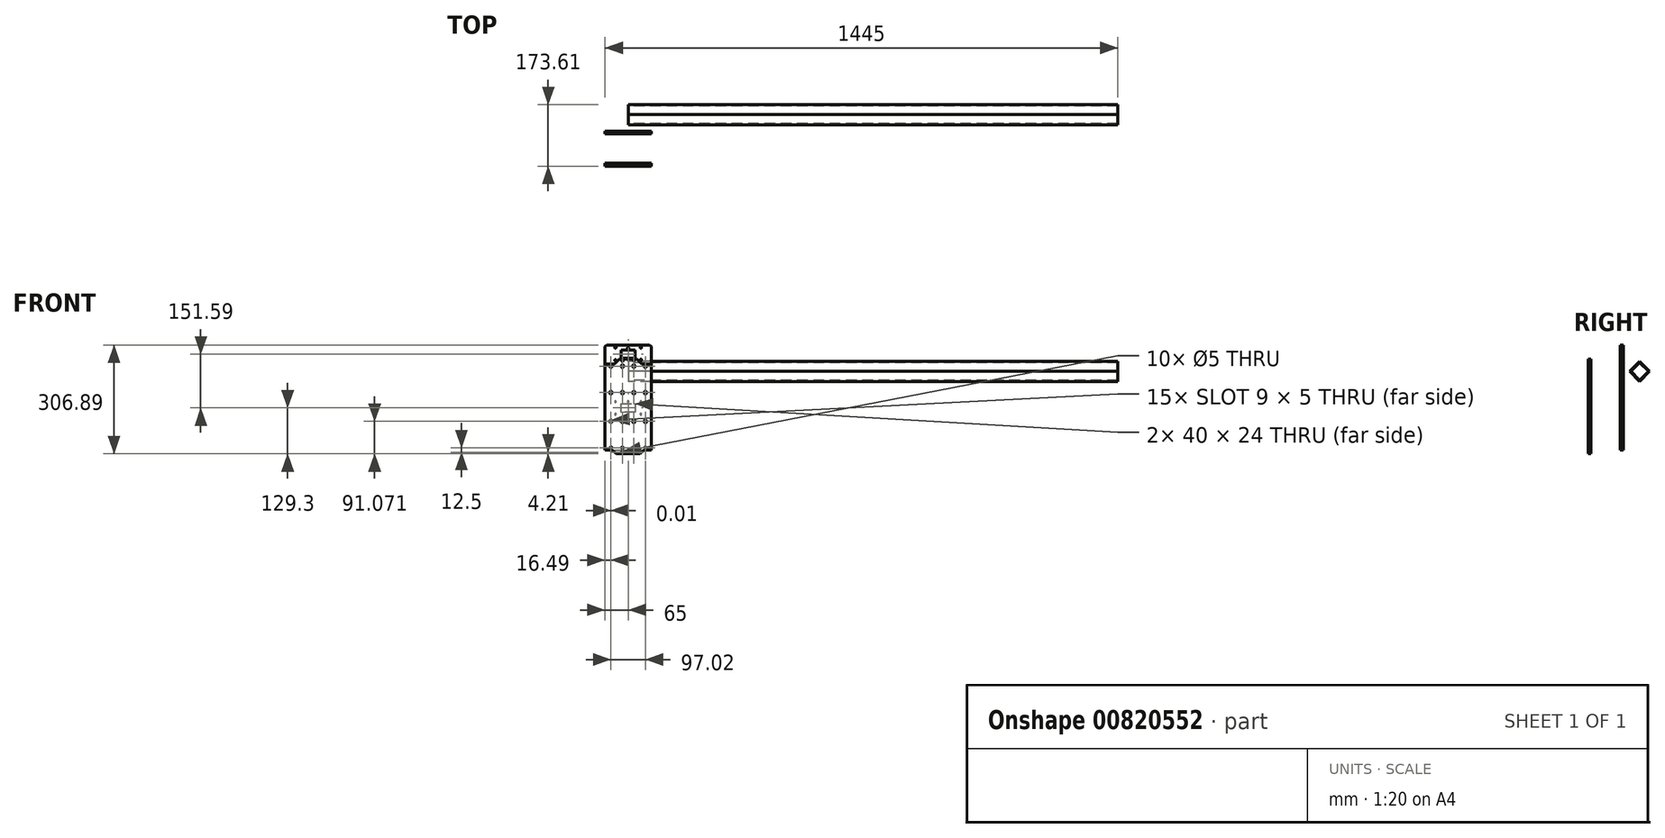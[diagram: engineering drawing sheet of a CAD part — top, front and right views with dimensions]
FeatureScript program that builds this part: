
annotation { "Feature Type Name" : "Feature", "Feature Type Description" : "" }
export const myFeature = defineFeature(function(context is Context, id is Id, definition is map)
    precondition{}
    {
        {
            var Q0;
            Q0=qCreatedBy(makeId("Front.planeOp"),FACE);
            var sketch = newSketch(context, id + "F0", { "sketchPlane" : qUnion([Q0])});
            skLineSegment(sketch, "E0", {"start": v(20, -14.5) * mm, "end": v(-20, -14.5) * mm});
            skLineSegment(sketch, "E1", {"start": v(20, 9.5) * mm, "end": v(20, -14.5) * mm});
            skLineSegment(sketch, "E2", {"start": v(-20, 9.5) * mm, "end": v(20, 9.5) * mm});
            skLineSegment(sketch, "E3", {"start": v(-20, -14.5) * mm, "end": v(-20, 9.5) * mm});
            skLineSegment(sketch, "E4", {"start": v(-51, 50.32) * mm, "end": v(-51, 47.32) * mm});
            skLineSegment(sketch, "E5", {"start": v(-46.01, 47.32) * mm, "end": v(-46.01, 50.32) * mm});
            skLineSegment(sketch, "E6", {"start": v(-18.67, 50.32) * mm, "end": v(-18.67, 47.32) * mm});
            skLineSegment(sketch, "E7", {"start": v(-13.67, 47.32) * mm, "end": v(-13.67, 50.32) * mm});
            skLineSegment(sketch, "E8", {"start": v(13.67, 50.32) * mm, "end": v(13.67, 47.32) * mm});
            skLineSegment(sketch, "E9", {"start": v(18.67, 47.32) * mm, "end": v(18.67, 50.32) * mm});
            skLineSegment(sketch, "E10", {"start": v(46, 50.32) * mm, "end": v(46, 47.32) * mm});
            skLineSegment(sketch, "E11", {"start": v(51, 47.32) * mm, "end": v(51, 50.32) * mm});
            skLineSegment(sketch, "E12", {"start": v(-51, 103.5) * mm, "end": v(-51, 100.5) * mm});
            skLineSegment(sketch, "E13", {"start": v(-46.01, 100.5) * mm, "end": v(-46.01, 103.5) * mm});
            skLineSegment(sketch, "E14", {"start": v(-13.67, 100.5) * mm, "end": v(-13.67, 103.5) * mm});
            skLineSegment(sketch, "E15", {"start": v(-18.67, 103.5) * mm, "end": v(-18.67, 100.5) * mm});
            skLineSegment(sketch, "E16", {"start": v(18.67, 100.5) * mm, "end": v(18.67, 103.5) * mm});
            skLineSegment(sketch, "E17", {"start": v(13.67, 103.5) * mm, "end": v(13.67, 100.5) * mm});
            skLineSegment(sketch, "E18", {"start": v(51, 100.5) * mm, "end": v(51, 103.5) * mm});
            skLineSegment(sketch, "E19", {"start": v(46, 103.5) * mm, "end": v(46, 100.5) * mm});
            skLineSegment(sketch, "E20", {"start": v(-46.01, -55.32) * mm, "end": v(-46.01, -52.32) * mm});
            skLineSegment(sketch, "E21", {"start": v(-51, -52.32) * mm, "end": v(-51, -55.32) * mm});
            skLineSegment(sketch, "E22", {"start": v(-13.67, -55.32) * mm, "end": v(-13.67, -52.32) * mm});
            skLineSegment(sketch, "E23", {"start": v(-18.67, -52.32) * mm, "end": v(-18.67, -55.32) * mm});
            skLineSegment(sketch, "E24", {"start": v(18.67, -55.32) * mm, "end": v(18.67, -52.32) * mm});
            skLineSegment(sketch, "E25", {"start": v(13.67, -52.32) * mm, "end": v(13.67, -55.32) * mm});
            skLineSegment(sketch, "E26", {"start": v(51, -55.32) * mm, "end": v(51, -52.32) * mm});
            skLineSegment(sketch, "E27", {"start": v(46, -52.32) * mm, "end": v(46, -55.32) * mm});
            skLineSegment(sketch, "E28", {"start": v(60, -113.5) * mm, "end": v(65, -108.5) * mm});
            skLineSegment(sketch, "E29", {"start": v(34, -124.5) * mm, "end": v(45, -113.5) * mm});
            skLineSegment(sketch, "E30", {"start": v(34, -124.5) * mm, "end": v(-34, -124.5) * mm});
            skLineSegment(sketch, "E31", {"start": v(-45, -113.5) * mm, "end": v(-34, -124.5) * mm});
            skLineSegment(sketch, "E32", {"start": v(-65, -108.5) * mm, "end": v(-60, -113.5) * mm});
            skLineSegment(sketch, "E33", {"start": v(-60, 110.5) * mm, "end": v(-65, 105.5) * mm});
            skLineSegment(sketch, "E34", {"start": v(-39, 110.5) * mm, "end": v(-60, 110.5) * mm});
            skLineSegment(sketch, "E35", {"start": v(-25, 124.5) * mm, "end": v(-39, 110.5) * mm});
            skLineSegment(sketch, "E36", {"start": v(-25, 124.5) * mm, "end": v(25, 124.5) * mm});
            skLineSegment(sketch, "E37", {"start": v(39, 110.5) * mm, "end": v(25, 124.5) * mm});
            skLineSegment(sketch, "E38", {"start": v(60, 110.5) * mm, "end": v(39, 110.5) * mm});
            skLineSegment(sketch, "E39", {"start": v(65, 105.5) * mm, "end": v(60, 110.5) * mm});
            skLineSegment(sketch, "E40", {"start": v(-65, 105.5) * mm, "end": v(-65, -108.5) * mm});
            skLineSegment(sketch, "E41", {"start": v(65, -108.5) * mm, "end": v(65, 105.5) * mm});
            skLineSegment(sketch, "E42", {"start": v(45, -113.5) * mm, "end": v(60, -113.5) * mm});
            skLineSegment(sketch, "E43", {"start": v(-60, -113.5) * mm, "end": v(-45, -113.5) * mm});
            skCircle(sketch, "E44", {"center": v(-48.5, -107) * mm, "radius": 2.5 * mm});
            skCircle(sketch, "E45", {"center": v(-16.17, -107) * mm, "radius": 2.5 * mm});
            skCircle(sketch, "E46", {"center": v(16.17, -107) * mm, "radius": 2.5 * mm});
            skCircle(sketch, "E47", {"center": v(48.5, -107) * mm, "radius": 2.5 * mm});
            skCircle(sketch, "E48", {"center": v(-36, 15) * mm, "radius": 2.05 * mm});
            skCircle(sketch, "E49", {"center": v(0, 15) * mm, "radius": 2.05 * mm});
            skCircle(sketch, "E50", {"center": v(36, 15) * mm, "radius": 2.05 * mm});
            skCircle(sketch, "E51", {"center": v(36, -20) * mm, "radius": 2.05 * mm});
            skCircle(sketch, "E52", {"center": v(0, -20) * mm, "radius": 2.05 * mm});
            skCircle(sketch, "E53", {"center": v(-36, -20) * mm, "radius": 2.05 * mm});
            skCircle(sketch, "E54", {"center": v(0, 119) * mm, "radius": 2.05 * mm});
            skCircle(sketch, "E55", {"center": v(16.17, -119.5) * mm, "radius": 2.5 * mm});
            skCircle(sketch, "E56", {"center": v(-16.17, -119.5) * mm, "radius": 2.5 * mm});
            skCircle(sketch, "E57", {"center": v(16.17, 119) * mm, "radius": 2.5 * mm});
            skCircle(sketch, "E58", {"center": v(-16.17, 119) * mm, "radius": 2.5 * mm});
            skCircle(sketch, "E59", {"center": v(50, -90) * mm, "radius": 2.25 * mm});
            skCircle(sketch, "E60", {"center": v(50, -65) * mm, "radius": 2.25 * mm});
            skCircle(sketch, "E61", {"center": v(-50, -90) * mm, "radius": 2.25 * mm});
            skCircle(sketch, "E62", {"center": v(-50, -65) * mm, "radius": 2.25 * mm});
            skCircle(sketch, "E63", {"center": v(-50, -40) * mm, "radius": 2.25 * mm});
            skCircle(sketch, "E64", {"center": v(-50, -15) * mm, "radius": 2.25 * mm});
            skCircle(sketch, "E65", {"center": v(50, -40) * mm, "radius": 2.25 * mm});
            skCircle(sketch, "E66", {"center": v(50, -15) * mm, "radius": 2.25 * mm});
            skCircle(sketch, "E67", {"center": v(50, 10) * mm, "radius": 2.25 * mm});
            skCircle(sketch, "E68", {"center": v(-50, 10) * mm, "radius": 2.25 * mm});
            skCircle(sketch, "E69", {"center": v(-50, 35) * mm, "radius": 2.25 * mm});
            skCircle(sketch, "E70", {"center": v(50, 35) * mm, "radius": 2.25 * mm});
            skCircle(sketch, "E71", {"center": v(50, 60) * mm, "radius": 2.25 * mm});
            skCircle(sketch, "E72", {"center": v(-50, 60) * mm, "radius": 2.25 * mm});
            skCircle(sketch, "E73", {"center": v(-50, 85) * mm, "radius": 2.25 * mm});
            skCircle(sketch, "E74", {"center": v(50, 85) * mm, "radius": 2.25 * mm});
            skArc(sketch, "E75", {"start": v(-51, 47.32) * mm, "mid": v(-48.5, 44.82) * mm, "end": v(-46, 47.32) * mm});
            skArc(sketch, "E76", {"start": v(-46, 50.32) * mm, "mid": v(-48.5, 52.82) * mm, "end": v(-51, 50.32) * mm});
            skArc(sketch, "E77", {"start": v(-18.67, 47.32) * mm, "mid": v(-16.17, 44.82) * mm, "end": v(-13.67, 47.32) * mm});
            skArc(sketch, "E78", {"start": v(-13.67, 50.32) * mm, "mid": v(-16.17, 52.82) * mm, "end": v(-18.67, 50.32) * mm});
            skArc(sketch, "E79", {"start": v(13.67, 47.32) * mm, "mid": v(16.17, 44.82) * mm, "end": v(18.67, 47.32) * mm});
            skArc(sketch, "E80", {"start": v(18.67, 50.32) * mm, "mid": v(16.17, 52.82) * mm, "end": v(13.67, 50.32) * mm});
            skArc(sketch, "E81", {"start": v(46, 47.32) * mm, "mid": v(48.5, 44.82) * mm, "end": v(51, 47.32) * mm});
            skArc(sketch, "E82", {"start": v(51, 50.32) * mm, "mid": v(48.5, 52.82) * mm, "end": v(46, 50.32) * mm});
            skArc(sketch, "E83", {"start": v(-51, 100.5) * mm, "mid": v(-48.5, 98) * mm, "end": v(-46, 100.5) * mm});
            skArc(sketch, "E84", {"start": v(-46, 103.5) * mm, "mid": v(-48.5, 106) * mm, "end": v(-51, 103.5) * mm});
            skArc(sketch, "E85", {"start": v(-18.67, 100.5) * mm, "mid": v(-16.17, 98) * mm, "end": v(-13.67, 100.5) * mm});
            skArc(sketch, "E86", {"start": v(-13.67, 103.5) * mm, "mid": v(-16.17, 106) * mm, "end": v(-18.67, 103.5) * mm});
            skArc(sketch, "E87", {"start": v(13.67, 100.5) * mm, "mid": v(16.17, 98) * mm, "end": v(18.67, 100.5) * mm});
            skArc(sketch, "E88", {"start": v(18.67, 103.5) * mm, "mid": v(16.17, 106) * mm, "end": v(13.67, 103.5) * mm});
            skArc(sketch, "E89", {"start": v(46, 100.5) * mm, "mid": v(48.5, 98) * mm, "end": v(51, 100.5) * mm});
            skArc(sketch, "E90", {"start": v(51, 103.5) * mm, "mid": v(48.5, 106) * mm, "end": v(46, 103.5) * mm});
            skArc(sketch, "E91", {"start": v(-51, -55.32) * mm, "mid": v(-48.5, -57.82) * mm, "end": v(-46, -55.32) * mm});
            skArc(sketch, "E92", {"start": v(-46, -52.32) * mm, "mid": v(-48.5, -49.82) * mm, "end": v(-51, -52.32) * mm});
            skArc(sketch, "E93", {"start": v(-18.67, -55.32) * mm, "mid": v(-16.17, -57.82) * mm, "end": v(-13.67, -55.32) * mm});
            skArc(sketch, "E94", {"start": v(-13.67, -52.32) * mm, "mid": v(-16.17, -49.82) * mm, "end": v(-18.67, -52.32) * mm});
            skArc(sketch, "E95", {"start": v(13.67, -55.32) * mm, "mid": v(16.17, -57.82) * mm, "end": v(18.67, -55.32) * mm});
            skArc(sketch, "E96", {"start": v(18.67, -52.32) * mm, "mid": v(16.17, -49.82) * mm, "end": v(13.67, -52.32) * mm});
            skArc(sketch, "E97", {"start": v(46, -55.32) * mm, "mid": v(48.5, -57.82) * mm, "end": v(51, -55.32) * mm});
            skArc(sketch, "E98", {"start": v(51, -52.32) * mm, "mid": v(48.5, -49.82) * mm, "end": v(46, -52.32) * mm});
            skSolve(sketch);
        }
        {
            var Q0;
            Q0=qCreatedBy(makeId("Right.planeOp"),FACE);
            var sketch = newSketch(context, id + "F1", { "sketchPlane" : qUnion([Q0])});
            skLineSegment(sketch, "E99.bottom", {"start": v(137.33, 128.79) * mm, "end": v(109.04, 100.5) * mm});
            skLineSegment(sketch, "E99.top", {"start": v(165.61, 100.5) * mm, "end": v(137.33, 72.22) * mm});
            skLineSegment(sketch, "E99.left", {"start": v(137.33, 128.79) * mm, "end": v(165.61, 100.5) * mm});
            skLineSegment(sketch, "E99.right", {"start": v(109.04, 100.5) * mm, "end": v(137.33, 72.22) * mm});
            skSolve(sketch);
        }
        {
            var Q0;
            Q0=qSketchRegion(id+"F1",true);
            extrude(context, id + "F2", {"entities" : qUnion([Q0]), "depth" : 1380 * mm, "offsetDistance" : 25 * mm});
        }
        {
            var Q0;
            Q0=makeQuery(id+"F2.opExtrude","CAP_FACE",FACE,{"disambiguationData":[OSD([sQuery(id+"F1.wireOp",EDGE,"E99.bottom"),sQuery(id+"F1.wireOp",EDGE,"E99.top"),sQuery(id+"F1.wireOp",EDGE,"E99.left"),sQuery(id+"F1.wireOp",EDGE,"E99.right")])],"isStart":true});
            var Q1;
            Q1=makeQuery(id+"F2.opExtrude","CAP_FACE",FACE,{"disambiguationData":[OSD([sQuery(id+"F1.wireOp",EDGE,"E99.bottom"),sQuery(id+"F1.wireOp",EDGE,"E99.top"),sQuery(id+"F1.wireOp",EDGE,"E99.left"),sQuery(id+"F1.wireOp",EDGE,"E99.right")])],"isStart":false});
            shell(context, id + "F3", {"entities" : qUnion([Q0, Q1]), "thickness" : 2.5 * mm});
        }
        {
            var Q0;
            Q0=qCreatedBy(makeId("Front.planeOp"),FACE);
            var sketch = newSketch(context, id + "F4", { "sketchPlane" : qUnion([Q0])});
            skLineSegment(sketch, "E100.bottom", {"start": v(65, 121.7) * mm, "end": v(-65, 121.7) * mm});
            skLineSegment(sketch, "E100.left", {"start": v(65, 121.7) * mm, "end": v(65, -121.7) * mm});
            skLineSegment(sketch, "E100.right", {"start": v(-65, 121.7) * mm, "end": v(-65, -121.7) * mm});
            skCircle(sketch, "E101", {"center": v(-48.5, -115.1) * mm, "radius": 2.5 * mm});
            skCircle(sketch, "E102", {"center": v(-16.18, -115.1) * mm, "radius": 2.5 * mm});
            skCircle(sketch, "E103", {"center": v(16.18, -115.1) * mm, "radius": 2.5 * mm});
            skCircle(sketch, "E104", {"center": v(48.5, -115.1) * mm, "radius": 2.5 * mm});
            skLineSegment(sketch, "E105", {"start": v(-48.5, -42.51) * mm, "end": v(-48.5, -38.51) * mm});
            skLineSegment(sketch, "E106", {"start": v(-16.18, -42.51) * mm, "end": v(-16.18, -38.51) * mm});
            skLineSegment(sketch, "E107", {"start": v(16.18, -42.51) * mm, "end": v(16.18, -38.51) * mm});
            skLineSegment(sketch, "E108", {"start": v(48.5, -42.51) * mm, "end": v(48.5, -38.51) * mm});
            skLineSegment(sketch, "E109.MirrorCS", {"start": v(16.18, 42.51) * mm, "end": v(16.18, 38.51) * mm});
            skLineSegment(sketch, "E110.MirrorCS", {"start": v(48.5, 42.51) * mm, "end": v(48.5, 38.51) * mm});
            skLineSegment(sketch, "E111.MirrorCS", {"start": v(-16.18, 42.51) * mm, "end": v(-16.18, 38.51) * mm});
            skLineSegment(sketch, "E112.MirrorCS", {"start": v(-48.5, 42.51) * mm, "end": v(-48.5, 38.51) * mm});
            skLineSegment(sketch, "E113", {"start": v(-48.5, 117.1) * mm, "end": v(-48.5, 113.1) * mm});
            skLineSegment(sketch, "E114", {"start": v(-16.18, 117.1) * mm, "end": v(-16.18, 113.1) * mm});
            skLineSegment(sketch, "E115", {"start": v(16.18, 117.1) * mm, "end": v(16.18, 113.1) * mm});
            skLineSegment(sketch, "E116", {"start": v(48.5, 117.1) * mm, "end": v(48.5, 113.1) * mm});
            skArc(sketch, "E117.0.startCap", {"start": v(-51, 117.1) * mm, "mid": v(-48.5, 119.6) * mm, "end": v(-46, 117.1) * mm});
            skArc(sketch, "E117.0.endCap", {"start": v(-46, 113.1) * mm, "mid": v(-48.5, 110.6) * mm, "end": v(-51, 113.1) * mm});
            skLineSegment(sketch, "E117.0.left", {"start": v(-46, 117.1) * mm, "end": v(-46, 113.1) * mm});
            skLineSegment(sketch, "E117.0.right", {"start": v(-51, 117.1) * mm, "end": v(-51, 113.1) * mm});
            skArc(sketch, "E117.1.startCap", {"start": v(-18.68, 117.1) * mm, "mid": v(-16.18, 119.6) * mm, "end": v(-13.68, 117.1) * mm});
            skArc(sketch, "E117.1.endCap", {"start": v(-13.68, 113.1) * mm, "mid": v(-16.18, 110.6) * mm, "end": v(-18.68, 113.1) * mm});
            skLineSegment(sketch, "E117.1.left", {"start": v(-13.68, 117.1) * mm, "end": v(-13.68, 113.1) * mm});
            skLineSegment(sketch, "E117.1.right", {"start": v(-18.68, 117.1) * mm, "end": v(-18.68, 113.1) * mm});
            skArc(sketch, "E117.2.startCap", {"start": v(13.68, 117.1) * mm, "mid": v(16.18, 119.6) * mm, "end": v(18.68, 117.1) * mm});
            skArc(sketch, "E117.2.endCap", {"start": v(18.68, 113.1) * mm, "mid": v(16.18, 110.6) * mm, "end": v(13.68, 113.1) * mm});
            skLineSegment(sketch, "E117.2.left", {"start": v(18.68, 117.1) * mm, "end": v(18.68, 113.1) * mm});
            skLineSegment(sketch, "E117.2.right", {"start": v(13.68, 117.1) * mm, "end": v(13.68, 113.1) * mm});
            skArc(sketch, "E117.3.startCap", {"start": v(46, 117.1) * mm, "mid": v(48.5, 119.6) * mm, "end": v(51, 117.1) * mm});
            skArc(sketch, "E117.3.endCap", {"start": v(51, 113.1) * mm, "mid": v(48.5, 110.6) * mm, "end": v(46, 113.1) * mm});
            skLineSegment(sketch, "E117.3.left", {"start": v(51, 117.1) * mm, "end": v(51, 113.1) * mm});
            skLineSegment(sketch, "E117.3.right", {"start": v(46, 117.1) * mm, "end": v(46, 113.1) * mm});
            skArc(sketch, "E117.4.startCap", {"start": v(-51, 42.51) * mm, "mid": v(-48.5, 45.01) * mm, "end": v(-46, 42.51) * mm});
            skArc(sketch, "E117.4.endCap", {"start": v(-46, 38.51) * mm, "mid": v(-48.5, 36.01) * mm, "end": v(-51, 38.51) * mm});
            skLineSegment(sketch, "E117.4.left", {"start": v(-46, 42.51) * mm, "end": v(-46, 38.51) * mm});
            skLineSegment(sketch, "E117.4.right", {"start": v(-51, 42.51) * mm, "end": v(-51, 38.51) * mm});
            skArc(sketch, "E117.5.startCap", {"start": v(-18.68, 42.51) * mm, "mid": v(-16.18, 45.01) * mm, "end": v(-13.68, 42.51) * mm});
            skArc(sketch, "E117.5.endCap", {"start": v(-13.68, 38.51) * mm, "mid": v(-16.18, 36.01) * mm, "end": v(-18.68, 38.51) * mm});
            skLineSegment(sketch, "E117.5.left", {"start": v(-13.68, 42.51) * mm, "end": v(-13.68, 38.51) * mm});
            skLineSegment(sketch, "E117.5.right", {"start": v(-18.68, 42.51) * mm, "end": v(-18.68, 38.51) * mm});
            skArc(sketch, "E117.6.startCap", {"start": v(13.68, 42.51) * mm, "mid": v(16.18, 45.01) * mm, "end": v(18.68, 42.51) * mm});
            skArc(sketch, "E117.6.endCap", {"start": v(18.68, 38.51) * mm, "mid": v(16.18, 36.01) * mm, "end": v(13.68, 38.51) * mm});
            skLineSegment(sketch, "E117.6.left", {"start": v(18.68, 42.51) * mm, "end": v(18.68, 38.51) * mm});
            skLineSegment(sketch, "E117.6.right", {"start": v(13.68, 42.51) * mm, "end": v(13.68, 38.51) * mm});
            skArc(sketch, "E117.7.startCap", {"start": v(46, 42.51) * mm, "mid": v(48.5, 45.01) * mm, "end": v(51, 42.51) * mm});
            skArc(sketch, "E117.7.endCap", {"start": v(51, 38.51) * mm, "mid": v(48.5, 36.01) * mm, "end": v(46, 38.51) * mm});
            skLineSegment(sketch, "E117.7.left", {"start": v(51, 42.51) * mm, "end": v(51, 38.51) * mm});
            skLineSegment(sketch, "E117.7.right", {"start": v(46, 42.51) * mm, "end": v(46, 38.51) * mm});
            skArc(sketch, "E117.8.startCap", {"start": v(51, -42.51) * mm, "mid": v(48.5, -45.01) * mm, "end": v(46, -42.51) * mm});
            skArc(sketch, "E117.8.endCap", {"start": v(46, -38.51) * mm, "mid": v(48.5, -36.01) * mm, "end": v(51, -38.51) * mm});
            skLineSegment(sketch, "E117.8.left", {"start": v(46, -42.51) * mm, "end": v(46, -38.51) * mm});
            skLineSegment(sketch, "E117.8.right", {"start": v(51, -42.51) * mm, "end": v(51, -38.51) * mm});
            skArc(sketch, "E117.9.startCap", {"start": v(18.68, -42.51) * mm, "mid": v(16.18, -45.01) * mm, "end": v(13.68, -42.51) * mm});
            skArc(sketch, "E117.9.endCap", {"start": v(13.68, -38.51) * mm, "mid": v(16.18, -36.01) * mm, "end": v(18.68, -38.51) * mm});
            skLineSegment(sketch, "E117.9.left", {"start": v(13.68, -42.51) * mm, "end": v(13.68, -38.51) * mm});
            skLineSegment(sketch, "E117.9.right", {"start": v(18.68, -42.51) * mm, "end": v(18.68, -38.51) * mm});
            skArc(sketch, "E117.10.startCap", {"start": v(-13.68, -42.51) * mm, "mid": v(-16.18, -45.01) * mm, "end": v(-18.68, -42.51) * mm});
            skArc(sketch, "E117.10.endCap", {"start": v(-18.68, -38.51) * mm, "mid": v(-16.18, -36.01) * mm, "end": v(-13.68, -38.51) * mm});
            skLineSegment(sketch, "E117.10.left", {"start": v(-18.68, -42.51) * mm, "end": v(-18.68, -38.51) * mm});
            skLineSegment(sketch, "E117.10.right", {"start": v(-13.68, -42.51) * mm, "end": v(-13.68, -38.51) * mm});
            skArc(sketch, "E117.11.startCap", {"start": v(-46, -42.51) * mm, "mid": v(-48.5, -45.01) * mm, "end": v(-51, -42.51) * mm});
            skArc(sketch, "E117.11.endCap", {"start": v(-51, -38.51) * mm, "mid": v(-48.5, -36.01) * mm, "end": v(-46, -38.51) * mm});
            skLineSegment(sketch, "E117.11.left", {"start": v(-51, -42.51) * mm, "end": v(-51, -38.51) * mm});
            skLineSegment(sketch, "E117.11.right", {"start": v(-46, -42.51) * mm, "end": v(-46, -38.51) * mm});
            skLineSegment(sketch, "E118", {"start": v(-39, 121.7) * mm, "end": v(-25, 135.7) * mm});
            skLineSegment(sketch, "E119", {"start": v(-25, 135.7) * mm, "end": v(25, 135.7) * mm});
            skLineSegment(sketch, "E120", {"start": v(25, 135.7) * mm, "end": v(39, 121.7) * mm});
            skLineSegment(sketch, "E121", {"start": v(39, 121.7) * mm, "end": v(39, 103.73) * mm, "construction": true});
            skLineSegment(sketch, "E122", {"start": v(25, 135.7) * mm, "end": v(25, 118.95) * mm, "construction": true});
            skLineSegment(sketch, "E123", {"start": v(-25, 135.7) * mm, "end": v(-25, 118.52) * mm, "construction": true});
            skLineSegment(sketch, "E124", {"start": v(-39, 121.7) * mm, "end": v(-39, 105.53) * mm, "construction": true});
            skLineSegment(sketch, "E125", {"start": v(-45, -121.7) * mm, "end": v(-45, -110.8) * mm, "construction": true});
            skLineSegment(sketch, "E126", {"start": v(-34, -131.8) * mm, "end": v(-34, -118.6) * mm, "construction": true});
            skLineSegment(sketch, "E127", {"start": v(34, -131.8) * mm, "end": v(34, -118.8) * mm, "construction": true});
            skLineSegment(sketch, "E128", {"start": v(45, -121.7) * mm, "end": v(45, -111) * mm, "construction": true});
            skCircle(sketch, "E129", {"center": v(-16.18, -127.6) * mm, "radius": 2.5 * mm});
            skCircle(sketch, "E130", {"center": v(16.18, -127.6) * mm, "radius": 2.5 * mm});
            skLineSegment(sketch, "E131", {"start": v(-65, -121.7) * mm, "end": v(-45, -121.7) * mm});
            skLineSegment(sketch, "E132", {"start": v(-34, -131.8) * mm, "end": v(-45, -121.7) * mm});
            skLineSegment(sketch, "E133", {"start": v(-34, -131.8) * mm, "end": v(34, -131.8) * mm});
            skLineSegment(sketch, "E134", {"start": v(34, -131.8) * mm, "end": v(45, -121.7) * mm});
            skLineSegment(sketch, "E135", {"start": v(45, -121.7) * mm, "end": v(65, -121.7) * mm});
            skCircle(sketch, "E136", {"center": v(-16.18, 130.74) * mm, "radius": 2.57 * mm});
            skCircle(sketch, "E137", {"center": v(16.18, 132.1) * mm, "radius": 2.49 * mm});
            skSolve(sketch);
        }
        {
            var Q0;
            Q0=makeQuery(id+"F4.imprint","IMPRINT",FACE,{"disambiguationData":[TD([[makeQuery(id+"F4.imprint","IMPRINT",EDGE,{"derivedFrom":sQuery(id+"F4.wireOp",EDGE,"E100.bottom")}),1.0]])]});
            var Q1;
            {var subQ0=sQuery(id+"F4.wireOp",EDGE,"E118");Q1=makeQuery(id+"F4.imprint","IMPRINT",FACE,{"disambiguationData":[TD([[makeQuery(id+"F4.imprint","IMPRINT",EDGE,{"derivedFrom":subQ0}),-1.0]])]});}
            var Q2;
            {var subQ0=sQuery(id+"F4.wireOp",EDGE,"JYC6ol7t-ZKkB-sm1I-73n9-ntt4Y6ct0uzj");Q2=makeQuery(id+"F4.imprint","IMPRINT",FACE,{"disambiguationData":[TD([[makeQuery(id+"F4.imprint","IMPRINT",EDGE,{"derivedFrom":subQ0}),1.0]])]});}
            extrude(context, id + "F5", {"entities" : qUnion([Q0, Q1, Q2]), "depth" : 8 * mm, "offsetDistance" : 25 * mm});
        }
        {
            var Q0;
            Q0=qCreatedBy(makeId("Front.planeOp"),FACE);
            cPlane(context, id + "F6", {"entities" : qUnion([Q0]), "cplaneType" : CPlaneType.OFFSET, "offset" : 83 * mm, "oppositeDirection" : true, "width" : 150 * mm, "height" : 150 * mm});
        }
        {
            var Q0;
            Q0=qCreatedBy(id+"F6.planeOp",FACE);
            var sketch = newSketch(context, id + "F7", { "sketchPlane" : qUnion([Q0])});
            skLineSegment(sketch, "E138", {"start": v(-60, 175.1) * mm, "end": v(-65, 170.1) * mm});
            skLineSegment(sketch, "E139", {"start": v(60, 175.1) * mm, "end": v(-60, 175.1) * mm});
            skLineSegment(sketch, "E140", {"start": v(65, 170.1) * mm, "end": v(60, 175.1) * mm});
            skLineSegment(sketch, "E141", {"start": v(60, -121.7) * mm, "end": v(65, -116.7) * mm});
            skLineSegment(sketch, "E142", {"start": v(-65, -116.7) * mm, "end": v(-60, -121.7) * mm});
            skLineSegment(sketch, "E143", {"start": v(20, -14.5) * mm, "end": v(-20, -14.5) * mm});
            skLineSegment(sketch, "E144", {"start": v(20, 9.5) * mm, "end": v(20, -14.5) * mm});
            skLineSegment(sketch, "E145", {"start": v(-20, 9.5) * mm, "end": v(20, 9.5) * mm});
            skLineSegment(sketch, "E146", {"start": v(-20, -14.5) * mm, "end": v(-20, 9.5) * mm});
            skLineSegment(sketch, "E147", {"start": v(-51, 42.51) * mm, "end": v(-51, 38.51) * mm});
            skLineSegment(sketch, "E148", {"start": v(-46, 38.51) * mm, "end": v(-46, 42.51) * mm});
            skLineSegment(sketch, "E149", {"start": v(-18.67, 42.51) * mm, "end": v(-18.67, 38.51) * mm});
            skLineSegment(sketch, "E150", {"start": v(-13.67, 38.51) * mm, "end": v(-13.67, 42.51) * mm});
            skLineSegment(sketch, "E151", {"start": v(13.67, 42.51) * mm, "end": v(13.67, 38.51) * mm});
            skLineSegment(sketch, "E152", {"start": v(18.67, 38.51) * mm, "end": v(18.67, 42.51) * mm});
            skLineSegment(sketch, "E153", {"start": v(46, 42.51) * mm, "end": v(46, 38.51) * mm});
            skLineSegment(sketch, "E154", {"start": v(51, 38.51) * mm, "end": v(51, 42.51) * mm});
            skLineSegment(sketch, "E155", {"start": v(-51, 117.1) * mm, "end": v(-51, 113.09) * mm});
            skLineSegment(sketch, "E156", {"start": v(-46, 113.09) * mm, "end": v(-46, 117.1) * mm});
            skLineSegment(sketch, "E157", {"start": v(-13.67, 113.09) * mm, "end": v(-13.67, 117.1) * mm});
            skLineSegment(sketch, "E158", {"start": v(-18.67, 117.1) * mm, "end": v(-18.67, 113.09) * mm});
            skLineSegment(sketch, "E159", {"start": v(18.67, 113.09) * mm, "end": v(18.67, 117.1) * mm});
            skLineSegment(sketch, "E160", {"start": v(13.67, 117.1) * mm, "end": v(13.67, 113.09) * mm});
            skLineSegment(sketch, "E161", {"start": v(51, 113.09) * mm, "end": v(51, 117.1) * mm});
            skLineSegment(sketch, "E162", {"start": v(46, 117.1) * mm, "end": v(46, 113.1) * mm});
            skLineSegment(sketch, "E163", {"start": v(-46, -42.73) * mm, "end": v(-46, -38.73) * mm});
            skLineSegment(sketch, "E164", {"start": v(-51, -38.73) * mm, "end": v(-51, -42.73) * mm});
            skLineSegment(sketch, "E165", {"start": v(-13.67, -42.73) * mm, "end": v(-13.67, -38.73) * mm});
            skLineSegment(sketch, "E166", {"start": v(-18.67, -38.73) * mm, "end": v(-18.67, -42.73) * mm});
            skLineSegment(sketch, "E167", {"start": v(18.67, -42.73) * mm, "end": v(18.67, -38.73) * mm});
            skLineSegment(sketch, "E168", {"start": v(13.67, -38.73) * mm, "end": v(13.67, -42.73) * mm});
            skLineSegment(sketch, "E169", {"start": v(51, -42.73) * mm, "end": v(51, -38.73) * mm});
            skLineSegment(sketch, "E170", {"start": v(46, -38.73) * mm, "end": v(46, -42.73) * mm});
            skLineSegment(sketch, "E171", {"start": v(20, 161.1) * mm, "end": v(-20, 161.1) * mm});
            skLineSegment(sketch, "E172", {"start": v(-20, 161.1) * mm, "end": v(-20, 137.1) * mm});
            skLineSegment(sketch, "E173", {"start": v(-20, 137.1) * mm, "end": v(20, 137.1) * mm});
            skLineSegment(sketch, "E174", {"start": v(20, 137.1) * mm, "end": v(20, 161.09) * mm});
            skLineSegment(sketch, "E175", {"start": v(-65, 170.1) * mm, "end": v(-65, -116.7) * mm});
            skLineSegment(sketch, "E176", {"start": v(65, -116.7) * mm, "end": v(65, 170.09) * mm});
            skLineSegment(sketch, "E177", {"start": v(-60, -121.7) * mm, "end": v(60, -121.7) * mm});
            skCircle(sketch, "E178", {"center": v(-48.5, -115.2) * mm, "radius": 2.5 * mm});
            skCircle(sketch, "E179", {"center": v(-16.17, -115.2) * mm, "radius": 2.5 * mm});
            skCircle(sketch, "E180", {"center": v(16.17, -115.2) * mm, "radius": 2.5 * mm});
            skCircle(sketch, "E181", {"center": v(48.5, -115.2) * mm, "radius": 2.5 * mm});
            skCircle(sketch, "E182", {"center": v(-36, 15) * mm, "radius": 2.05 * mm});
            skCircle(sketch, "E183", {"center": v(0, 15) * mm, "radius": 2.05 * mm});
            skCircle(sketch, "E184", {"center": v(36, 15) * mm, "radius": 2.05 * mm});
            skCircle(sketch, "E185", {"center": v(36, -20) * mm, "radius": 2.05 * mm});
            skCircle(sketch, "E186", {"center": v(0, -20) * mm, "radius": 2.05 * mm});
            skCircle(sketch, "E187", {"center": v(-36, -20) * mm, "radius": 2.05 * mm});
            skCircle(sketch, "E188", {"center": v(-36, 167.6) * mm, "radius": 2.05 * mm});
            skCircle(sketch, "E189", {"center": v(0, 166.6) * mm, "radius": 2.05 * mm});
            skCircle(sketch, "E190", {"center": v(36, 167.6) * mm, "radius": 2.05 * mm});
            skCircle(sketch, "E191", {"center": v(36, 132.6) * mm, "radius": 2.05 * mm});
            skCircle(sketch, "E192", {"center": v(0, 131.59) * mm, "radius": 2.05 * mm});
            skCircle(sketch, "E193", {"center": v(-36, 131.59) * mm, "radius": 2.05 * mm});
            skArc(sketch, "E194", {"start": v(-51, 38.51) * mm, "mid": v(-48.5, 36.01) * mm, "end": v(-46, 38.51) * mm});
            skArc(sketch, "E195", {"start": v(-45.97, 42.51) * mm, "mid": v(-48.47, 45.01) * mm, "end": v(-50.97, 42.51) * mm});
            skArc(sketch, "E196", {"start": v(-18.67, 38.51) * mm, "mid": v(-16.17, 36.01) * mm, "end": v(-13.67, 38.51) * mm});
            skArc(sketch, "E197", {"start": v(-13.64, 42.51) * mm, "mid": v(-16.14, 45.01) * mm, "end": v(-18.64, 42.51) * mm});
            skArc(sketch, "E198", {"start": v(13.67, 38.51) * mm, "mid": v(16.17, 36.01) * mm, "end": v(18.67, 38.51) * mm});
            skArc(sketch, "E199", {"start": v(18.7, 42.51) * mm, "mid": v(16.2, 45.01) * mm, "end": v(13.7, 42.51) * mm});
            skArc(sketch, "E200", {"start": v(46.01, 38.51) * mm, "mid": v(48.51, 36.01) * mm, "end": v(51, 38.51) * mm});
            skArc(sketch, "E201", {"start": v(51.05, 42.51) * mm, "mid": v(48.55, 45.01) * mm, "end": v(46.05, 42.51) * mm});
            skArc(sketch, "E202", {"start": v(-51, 113.1) * mm, "mid": v(-48.5, 110.6) * mm, "end": v(-46, 113.1) * mm});
            skArc(sketch, "E203", {"start": v(-46, 117.1) * mm, "mid": v(-48.5, 119.6) * mm, "end": v(-51, 117.1) * mm});
            skArc(sketch, "E204", {"start": v(-18.67, 113.1) * mm, "mid": v(-16.17, 110.6) * mm, "end": v(-13.67, 113.1) * mm});
            skArc(sketch, "E205", {"start": v(-13.67, 117.1) * mm, "mid": v(-16.17, 119.6) * mm, "end": v(-18.67, 117.1) * mm});
            skArc(sketch, "E206", {"start": v(13.68, 113.1) * mm, "mid": v(16.18, 110.6) * mm, "end": v(18.68, 113.1) * mm});
            skArc(sketch, "E207", {"start": v(18.65, 117.1) * mm, "mid": v(16.15, 119.6) * mm, "end": v(13.65, 117.1) * mm});
            skArc(sketch, "E208", {"start": v(46, 113.1) * mm, "mid": v(48.5, 110.6) * mm, "end": v(51, 113.1) * mm});
            skArc(sketch, "E209", {"start": v(51, 117.1) * mm, "mid": v(48.5, 119.6) * mm, "end": v(46, 117.1) * mm});
            skArc(sketch, "E210", {"start": v(-51, -42.73) * mm, "mid": v(-48.5, -45.23) * mm, "end": v(-46, -42.73) * mm});
            skArc(sketch, "E211", {"start": v(-46.02, -38.73) * mm, "mid": v(-48.52, -36.23) * mm, "end": v(-51.02, -38.73) * mm});
            skArc(sketch, "E212", {"start": v(-18.67, -42.73) * mm, "mid": v(-16.17, -45.23) * mm, "end": v(-13.67, -42.73) * mm});
            skArc(sketch, "E213", {"start": v(-13.68, -38.73) * mm, "mid": v(-16.18, -36.23) * mm, "end": v(-18.68, -38.73) * mm});
            skArc(sketch, "E214", {"start": v(13.67, -42.73) * mm, "mid": v(16.17, -45.23) * mm, "end": v(18.67, -42.73) * mm});
            skArc(sketch, "E215", {"start": v(18.65, -38.73) * mm, "mid": v(16.15, -36.23) * mm, "end": v(13.65, -38.73) * mm});
            skArc(sketch, "E216", {"start": v(45.97, -42.73) * mm, "mid": v(48.47, -45.23) * mm, "end": v(50.97, -42.73) * mm});
            skArc(sketch, "E217", {"start": v(51, -38.73) * mm, "mid": v(48.5, -36.23) * mm, "end": v(46, -38.73) * mm});
            skLineSegment(sketch, "E218.bottom", {"start": v(46, 117.1) * mm, "end": v(51, 117.1) * mm});
            skLineSegment(sketch, "E218.top", {"start": v(46, 113.1) * mm, "end": v(51, 113.1) * mm});
            skLineSegment(sketch, "E218.right", {"start": v(51, 117.1) * mm, "end": v(51, 113.1) * mm});
            skLineSegment(sketch, "E219.bottom", {"start": v(13.67, 117.1) * mm, "end": v(18.68, 117.1) * mm});
            skLineSegment(sketch, "E219.top", {"start": v(13.67, 113.1) * mm, "end": v(18.68, 113.1) * mm});
            skLineSegment(sketch, "E219.left", {"start": v(13.67, 117.1) * mm, "end": v(13.67, 113.1) * mm});
            skLineSegment(sketch, "E219.right", {"start": v(18.68, 117.1) * mm, "end": v(18.68, 113.1) * mm});
            skLineSegment(sketch, "E220.bottom", {"start": v(-18.67, 117.1) * mm, "end": v(-13.67, 117.1) * mm});
            skLineSegment(sketch, "E220.top", {"start": v(-18.67, 113.1) * mm, "end": v(-13.67, 113.1) * mm});
            skLineSegment(sketch, "E220.left", {"start": v(-18.67, 117.1) * mm, "end": v(-18.67, 113.1) * mm});
            skLineSegment(sketch, "E220.right", {"start": v(-13.67, 117.1) * mm, "end": v(-13.67, 113.1) * mm});
            skLineSegment(sketch, "E221.bottom", {"start": v(-51, 117.1) * mm, "end": v(-46, 117.1) * mm});
            skLineSegment(sketch, "E221.top", {"start": v(-51, 113.1) * mm, "end": v(-46, 113.1) * mm});
            skLineSegment(sketch, "E221.left", {"start": v(-51, 117.1) * mm, "end": v(-51, 113.1) * mm});
            skLineSegment(sketch, "E221.right", {"start": v(-46, 117.1) * mm, "end": v(-46, 113.1) * mm});
            skCircle(sketch, "E222", {"center": v(-48.5, 117.1) * mm, "radius": 2.5 * mm});
            skCircle(sketch, "E223", {"center": v(-48.5, 113.1) * mm, "radius": 2.5 * mm});
            skCircle(sketch, "E224", {"center": v(-16.17, 117.1) * mm, "radius": 2.5 * mm});
            skCircle(sketch, "E225", {"center": v(-16.17, 113.1) * mm, "radius": 2.5 * mm});
            skCircle(sketch, "E226", {"center": v(16.15, 117.1) * mm, "radius": 2.5 * mm});
            skCircle(sketch, "E227", {"center": v(16.18, 113.1) * mm, "radius": 2.5 * mm});
            skCircle(sketch, "E228", {"center": v(48.5, 117.1) * mm, "radius": 2.5 * mm});
            skCircle(sketch, "E229", {"center": v(48.5, 113.1) * mm, "radius": 2.5 * mm});
            skLineSegment(sketch, "E230.bottom", {"start": v(-50.97, 42.51) * mm, "end": v(-46, 42.51) * mm});
            skLineSegment(sketch, "E230.top", {"start": v(-50.97, 38.51) * mm, "end": v(-46, 38.51) * mm});
            skLineSegment(sketch, "E230.left", {"start": v(-50.97, 42.51) * mm, "end": v(-50.97, 38.51) * mm});
            skLineSegment(sketch, "E230.right", {"start": v(-46, 42.51) * mm, "end": v(-46, 38.51) * mm});
            skLineSegment(sketch, "E231.bottom", {"start": v(-18.64, 42.51) * mm, "end": v(-13.67, 42.51) * mm});
            skLineSegment(sketch, "E231.top", {"start": v(-18.64, 38.51) * mm, "end": v(-13.67, 38.51) * mm});
            skLineSegment(sketch, "E231.left", {"start": v(-18.64, 42.51) * mm, "end": v(-18.64, 38.51) * mm});
            skLineSegment(sketch, "E231.right", {"start": v(-13.67, 42.51) * mm, "end": v(-13.67, 38.51) * mm});
            skLineSegment(sketch, "E232.bottom", {"start": v(13.7, 42.51) * mm, "end": v(18.67, 42.51) * mm});
            skLineSegment(sketch, "E232.top", {"start": v(13.7, 38.51) * mm, "end": v(18.67, 38.51) * mm});
            skLineSegment(sketch, "E232.left", {"start": v(13.7, 42.51) * mm, "end": v(13.7, 38.51) * mm});
            skLineSegment(sketch, "E232.right", {"start": v(18.67, 42.51) * mm, "end": v(18.67, 38.51) * mm});
            skLineSegment(sketch, "E233.bottom", {"start": v(46.05, 42.51) * mm, "end": v(51, 42.51) * mm});
            skLineSegment(sketch, "E233.top", {"start": v(46.05, 38.51) * mm, "end": v(51, 38.51) * mm});
            skLineSegment(sketch, "E233.left", {"start": v(46.05, 42.51) * mm, "end": v(46.05, 38.51) * mm});
            skLineSegment(sketch, "E233.right", {"start": v(51, 42.51) * mm, "end": v(51, 38.51) * mm});
            skCircle(sketch, "E234", {"center": v(-48.47, 42.51) * mm, "radius": 2.5 * mm});
            skCircle(sketch, "E235", {"center": v(-48.5, 38.51) * mm, "radius": 2.5 * mm});
            skCircle(sketch, "E236", {"center": v(-16.14, 42.51) * mm, "radius": 2.5 * mm});
            skCircle(sketch, "E237", {"center": v(-16.17, 38.51) * mm, "radius": 2.5 * mm});
            skCircle(sketch, "E238", {"center": v(16.2, 42.51) * mm, "radius": 2.5 * mm});
            skCircle(sketch, "E239", {"center": v(16.17, 38.51) * mm, "radius": 2.5 * mm});
            skCircle(sketch, "E240", {"center": v(48.55, 42.51) * mm, "radius": 2.5 * mm});
            skCircle(sketch, "E241", {"center": v(48.51, 38.51) * mm, "radius": 2.5 * mm});
            skCircle(sketch, "E242", {"center": v(48.5, -38.73) * mm, "radius": 2.5 * mm});
            skCircle(sketch, "E243", {"center": v(48.47, -42.73) * mm, "radius": 2.54 * mm});
            skCircle(sketch, "E244", {"center": v(16.17, -42.73) * mm, "radius": 2.5 * mm});
            skCircle(sketch, "E245", {"center": v(16.15, -38.73) * mm, "radius": 2.5 * mm});
            skCircle(sketch, "E246", {"center": v(-16.18, -38.73) * mm, "radius": 2.5 * mm});
            skCircle(sketch, "E247", {"center": v(-16.17, -42.73) * mm, "radius": 2.5 * mm});
            skCircle(sketch, "E248", {"center": v(-48.52, -38.73) * mm, "radius": 2.5 * mm});
            skCircle(sketch, "E249", {"center": v(-48.5, -42.73) * mm, "radius": 2.5 * mm});
            skLineSegment(sketch, "E250.bottom", {"start": v(-51, -38.73) * mm, "end": v(-46, -38.73) * mm});
            skLineSegment(sketch, "E250.top", {"start": v(-51, -42.73) * mm, "end": v(-46, -42.73) * mm});
            skLineSegment(sketch, "E250.right", {"start": v(-46, -38.73) * mm, "end": v(-46, -42.73) * mm});
            skLineSegment(sketch, "E251.bottom", {"start": v(-18.67, -38.73) * mm, "end": v(-13.67, -38.73) * mm});
            skLineSegment(sketch, "E251.top", {"start": v(-18.67, -42.73) * mm, "end": v(-13.67, -42.73) * mm});
            skLineSegment(sketch, "E251.right", {"start": v(-13.67, -38.73) * mm, "end": v(-13.67, -42.73) * mm});
            skLineSegment(sketch, "E252.bottom", {"start": v(13.67, -38.73) * mm, "end": v(18.67, -38.73) * mm});
            skLineSegment(sketch, "E252.top", {"start": v(13.67, -42.73) * mm, "end": v(18.67, -42.73) * mm});
            skLineSegment(sketch, "E252.right", {"start": v(18.67, -38.73) * mm, "end": v(18.67, -42.73) * mm});
            skLineSegment(sketch, "E253.bottom", {"start": v(46, -38.73) * mm, "end": v(51, -38.73) * mm});
            skLineSegment(sketch, "E253.top", {"start": v(46, -42.73) * mm, "end": v(51, -42.73) * mm});
            skLineSegment(sketch, "E253.right", {"start": v(51, -38.73) * mm, "end": v(51, -42.73) * mm});
            skSolve(sketch);
        }
        {
            var Q0;
            Q0=qSketchRegion(id+"F7",true);
            extrude(context, id + "F8", {"entities" : qUnion([Q0]), "oppositeDirection" : true, "depth" : 8 * mm, "offsetDistance" : 25 * mm});
        }
    });
